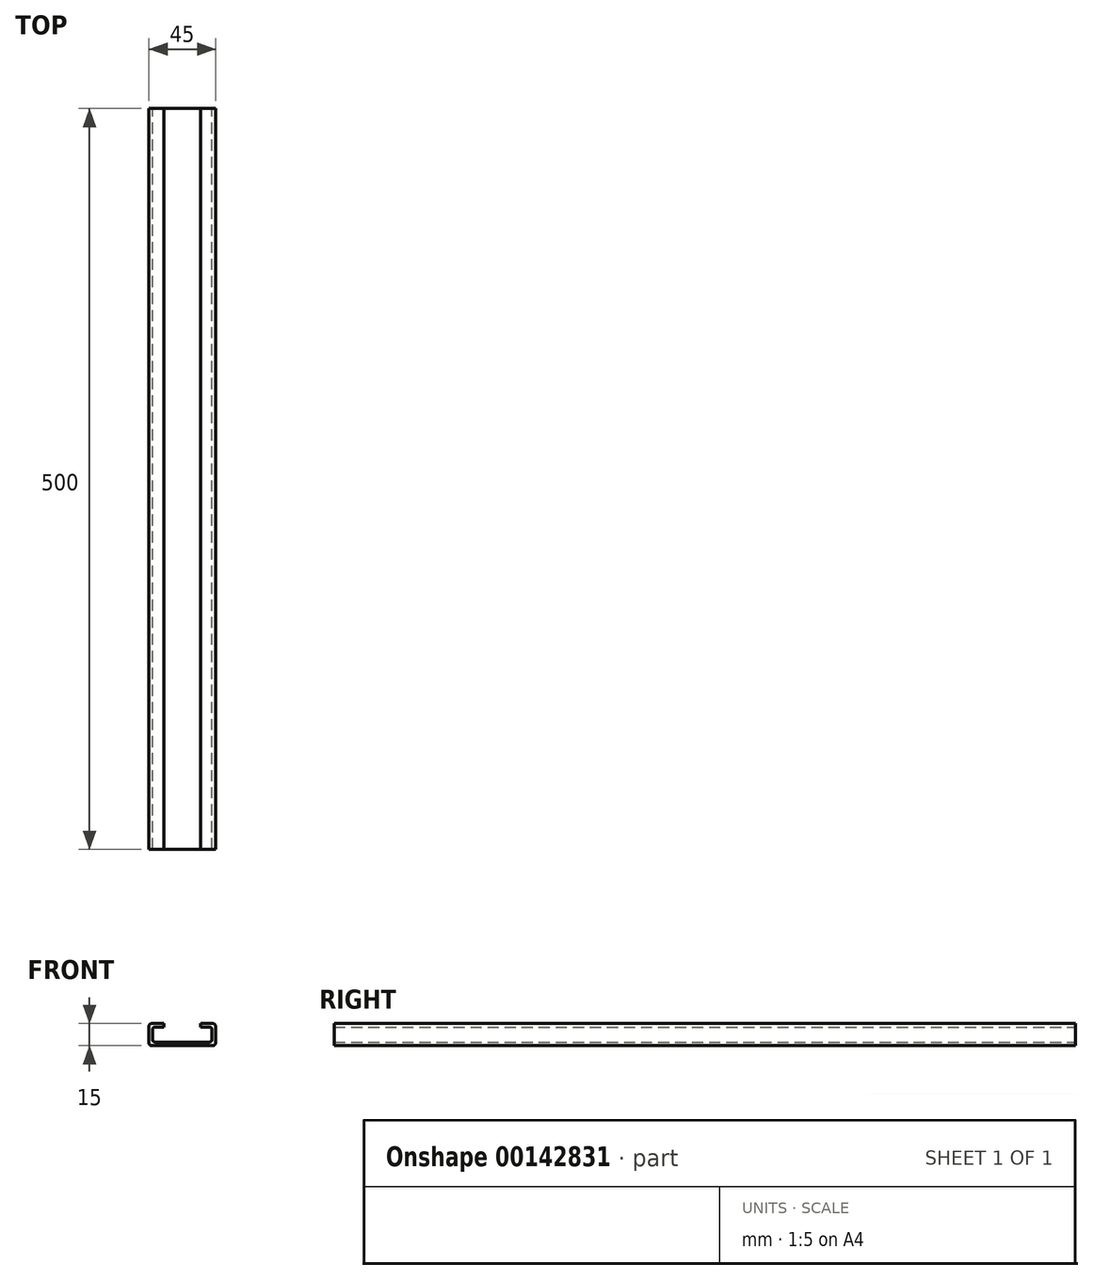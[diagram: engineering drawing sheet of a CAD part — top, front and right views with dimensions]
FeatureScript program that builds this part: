
annotation { "Feature Type Name" : "Feature", "Feature Type Description" : "" }
export const myFeature = defineFeature(function(context is Context, id is Id, definition is map)
    precondition{}
    {
        {
            var Q0;
            Q0=qCreatedBy(makeId("Front.planeOp"),FACE);
            var sketch = newSketch(context, id + "F0", { "sketchPlane" : qUnion([Q0])});
            skLineSegment(sketch, "E0.bottom", {"start": v(-22.5, 18.56) * mm, "end": v(-12.5, 18.56) * mm});
            skLineSegment(sketch, "E0.top", {"start": v(-22.5, 3.56) * mm, "end": v(22.5, 3.56) * mm});
            skLineSegment(sketch, "E0.left", {"start": v(-22.5, 18.56) * mm, "end": v(-22.5, 3.56) * mm});
            skLineSegment(sketch, "E0.right", {"start": v(22.5, 18.56) * mm, "end": v(22.5, 3.56) * mm});
            skLineSegment(sketch, "E1.bottom", {"start": v(-20, 16.06) * mm, "end": v(-12.5, 16.06) * mm});
            skLineSegment(sketch, "E1.top", {"start": v(-20, 6.06) * mm, "end": v(20, 6.06) * mm});
            skLineSegment(sketch, "E1.left", {"start": v(-20, 16.06) * mm, "end": v(-20, 6.06) * mm});
            skLineSegment(sketch, "E1.right", {"start": v(20, 16.06) * mm, "end": v(20, 6.06) * mm});
            skLineSegment(sketch, "E2", {"start": v(-12.5, 18.56) * mm, "end": v(-12.5, 16.06) * mm});
            skLineSegment(sketch, "E3", {"start": v(12.5, 18.56) * mm, "end": v(12.5, 16.06) * mm});
            skLineSegment(sketch, "E4.trimOffspring", {"start": v(12.5, 16.06) * mm, "end": v(20, 16.06) * mm});
            skLineSegment(sketch, "E5.trimOffspring", {"start": v(12.5, 18.56) * mm, "end": v(22.5, 18.56) * mm});
            skSolve(sketch);
        }
        {
            var Q0;
            Q0 = qSketchRegion(id + "F0", true);
            extrude(context, id + "F1", {"entities" : qUnion([Q0]), "depth" : 500 * mm, "offsetDistance" : 25 * mm});
        }
        {
            var Q0;
            Q0=makeQuery(id+"F1.opExtrude","SWEPT_EDGE",EDGE,{"disambiguationData":[OSD([sQuery(id+"F0.wireOp",EDGE,"E0.right"),sQuery(id+"F0.wireOp",EDGE,"E5.trimOffspring")])]});
            var Q1;
            Q1=makeQuery(id+"F1.opExtrude","SWEPT_EDGE",EDGE,{"disambiguationData":[OSD([sQuery(id+"F0.wireOp",EDGE,"E0.bottom"),sQuery(id+"F0.wireOp",EDGE,"E0.left")])]});
            var Q2;
            Q2=makeQuery(id+"F1.opExtrude","SWEPT_EDGE",EDGE,{"disambiguationData":[OSD([sQuery(id+"F0.wireOp",EDGE,"E0.top"),sQuery(id+"F0.wireOp",EDGE,"E0.left")])]});
            var Q3;
            Q3=makeQuery(id+"F1.opExtrude","SWEPT_EDGE",EDGE,{"disambiguationData":[OSD([sQuery(id+"F0.wireOp",EDGE,"E0.top"),sQuery(id+"F0.wireOp",EDGE,"E0.right")])]});
            fillet(context, id + "F2", {"entities" : qUnion([Q0, Q1, Q2, Q3]), "radius" : 2 * mm, "tangentPropagation" : true, "allowEdgeOverflow" : false});
        }
        {
            var Q0;
            Q0=makeQuery(id+"F1.opExtrude","SWEPT_EDGE",EDGE,{"disambiguationData":[OSD([sQuery(id+"F0.wireOp",EDGE,"E1.right"),sQuery(id+"F0.wireOp",EDGE,"E4.trimOffspring")])]});
            var Q1;
            Q1=makeQuery(id+"F1.opExtrude","SWEPT_EDGE",EDGE,{"disambiguationData":[OSD([sQuery(id+"F0.wireOp",EDGE,"E1.bottom"),sQuery(id+"F0.wireOp",EDGE,"E1.left")])]});
            fillet(context, id + "F3", {"entities" : qUnion([Q0, Q1]), "radius" : 1.5 * mm, "tangentPropagation" : true, "allowEdgeOverflow" : false});
        }
        {
            var Q0;
            Q0=makeQuery(id+"F1.opExtrude","SWEPT_EDGE",EDGE,{"disambiguationData":[OSD([sQuery(id+"F0.wireOp",EDGE,"E1.top"),sQuery(id+"F0.wireOp",EDGE,"E1.left")])]});
            var Q1;
            Q1=makeQuery(id+"F1.opExtrude","SWEPT_EDGE",EDGE,{"disambiguationData":[OSD([sQuery(id+"F0.wireOp",EDGE,"E1.top"),sQuery(id+"F0.wireOp",EDGE,"E1.right")])]});
            fillet(context, id + "F4", {"entities" : qUnion([Q0, Q1]), "radius" : 1.5 * mm, "tangentPropagation" : true, "allowEdgeOverflow" : false});
        }
    });
